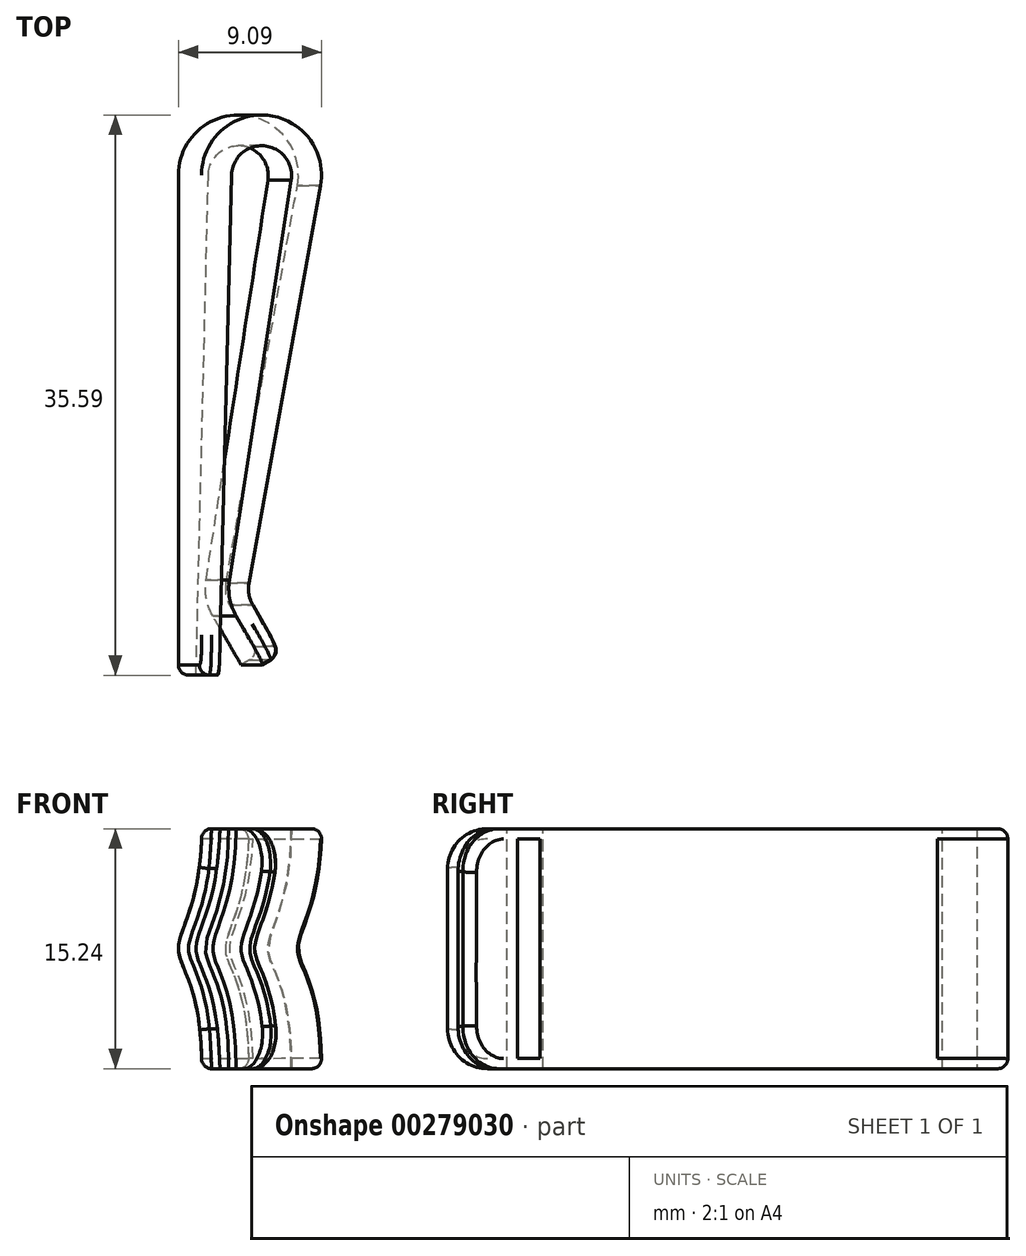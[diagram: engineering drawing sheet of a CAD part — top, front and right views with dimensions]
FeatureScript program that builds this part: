
annotation { "Feature Type Name" : "Feature", "Feature Type Description" : "" }
export const myFeature = defineFeature(function(context is Context, id is Id, definition is map)
    precondition{}
    {
        {
            var Q0;
            Q0=qCreatedBy(makeId("Top.planeOp"),FACE);
            var sketch = newSketch(context, id + "F0", { "sketchPlane" : qUnion([Q0])});
            skLineSegment(sketch, "E0", {"start": v(0, 0) * mm, "end": v(0, 31.75) * mm});
            skArc(sketch, "E1", {"start": v(0, 31.75) * mm, "mid": v(4.15, 35.54) * mm, "end": v(7.56, 31.07) * mm});
            skLineSegment(sketch, "E2", {"start": v(7.56, 31.07) * mm, "end": v(3.01, 5.83) * mm});
            skLineSegment(sketch, "E3", {"start": v(5.08, 1.27) * mm, "end": v(3.26, 4.42) * mm});
            skArc(sketch, "E4", {"start": v(3.01, 5.83) * mm, "mid": v(3.01, 5.1) * mm, "end": v(3.26, 4.42) * mm});
            skLineSegment(sketch, "E5", {"start": v(5.68, 31.41) * mm, "end": v(1.76, 6.03) * mm});
            skArc(sketch, "E6", {"start": v(1.76, 6.03) * mm, "mid": v(1.78, 4.85) * mm, "end": v(2.19, 3.74) * mm});
            skLineSegment(sketch, "E7", {"start": v(2.19, 3.74) * mm, "end": v(3.98, 0.64) * mm});
            skLineSegment(sketch, "E8", {"start": v(3.98, 0.63) * mm, "end": v(5.08, 1.27) * mm});
            skLineSegment(sketch, "E9", {"start": v(0, 0) * mm, "end": v(1.12, -0.03) * mm});
            skLineSegment(sketch, "E10", {"start": v(1.76, 6.03) * mm, "end": v(3.01, 5.83) * mm, "construction": true});
            skArc(sketch, "E11", {"start": v(1.9, 31.75) * mm, "mid": v(3.97, 33.6) * mm, "end": v(5.68, 31.41) * mm});
            skLineSegment(sketch, "E12", {"start": v(1.12, -0.03) * mm, "end": v(1.9, 31.75) * mm});
            skLineSegment(sketch, "E13", {"start": v(0, 31.75) * mm, "end": v(1.9, 31.75) * mm, "construction": true});
            skLineSegment(sketch, "E14", {"start": v(7.56, 31.07) * mm, "end": v(5.68, 31.41) * mm, "construction": true});
            skSolve(sketch);
        }
        {
            var Q0;
            Q0=qCreatedBy(makeId("Front.planeOp"),FACE);
            var sketch = newSketch(context, id + "F1", { "sketchPlane" : qUnion([Q0])});
            skFitSpline(sketch, "E15", {"points": [v(0, 0) * mm, v(-1.48, 7.62) * mm, v(0, 15.24) * mm], "startDerivative": vector(0, 32.76) * mm, "endDerivative": vector(0, 28.32) * mm});
            skSolve(sketch);
        }
        {
            var Q0;
            Q0 = qSketchRegion(id + "F0", true);
            var Q1;
            Q1 = qConstructionFilter(qBodyType(qCreatedBy(id + "F0" ,EDGE), BodyType.WIRE), ConstructionObject.NO);
            var Q2;
            Q2 = qConstructionFilter(qBodyType(qCreatedBy(id + "F1" ,EDGE), BodyType.WIRE), ConstructionObject.NO);
            sweep(context, id + "F2", {"profiles" : qUnion([Q0]), "surfaceProfiles" : qUnion([Q1]), "path" : qUnion([Q2]), "keepProfileOrientation" : true});
        }
        {
            var Q0;
            Q0=makeQuery(id+"F2.opSweep","CAP_EDGE",EDGE,{"disambiguationData":[OSD([sQuery(id+"F0.wireOp",EDGE,"E8"),sQuery(id+"F1.wireOp",VERTEX,"E15.end")])],"isStart":false});
            var Q1;
            Q1=makeQuery(id+"F2.opSweep","CAP_EDGE",EDGE,{"disambiguationData":[OSD([sQuery(id+"F0.wireOp",EDGE,"E8"),sQuery(id+"F1.wireOp",VERTEX,"E15.start")])],"isStart":true});
            var Q2;
            Q2=makeQuery(id+"F2.opSweep","CAP_EDGE",EDGE,{"disambiguationData":[OSD([sQuery(id+"F0.wireOp",EDGE,"E9"),sQuery(id+"F1.wireOp",VERTEX,"E15.end")])],"isStart":false});
            var Q3;
            Q3=makeQuery(id+"F2.opSweep","CAP_EDGE",EDGE,{"disambiguationData":[OSD([sQuery(id+"F0.wireOp",EDGE,"E9"),sQuery(id+"F1.wireOp",VERTEX,"E15.start")])],"isStart":true});
            fillet(context, id + "F3", {"entities" : qUnion([Q0, Q1, Q2, Q3]), "radius" : 2.54 * mm, "tangentPropagation" : true, "allowEdgeOverflow" : false});
        }
        {
            var Q0;
            Q0=makeQuery(id+"F2.opSweep","CAP_EDGE",EDGE,{"disambiguationData":[OSD([sQuery(id+"F0.wireOp",EDGE,"E2"),sQuery(id+"F1.wireOp",VERTEX,"E15.end")])],"isStart":false});
            var Q1;
            Q1=makeQuery(id+"F2.opSweep","CAP_EDGE",EDGE,{"disambiguationData":[OSD([sQuery(id+"F0.wireOp",EDGE,"E1"),sQuery(id+"F1.wireOp",VERTEX,"E15.end")])],"isStart":false});
            var Q2;
            Q2=makeQuery(id+"F2.opSweep","CAP_EDGE",EDGE,{"disambiguationData":[OSD([sQuery(id+"F0.wireOp",EDGE,"E0"),sQuery(id+"F1.wireOp",VERTEX,"E15.end")])],"isStart":false});
            fillet(context, id + "F4", {"entities" : qUnion([Q0, Q1, Q2]), "radius" : 0.64 * mm, "tangentPropagation" : true, "allowEdgeOverflow" : false});
        }
    });
